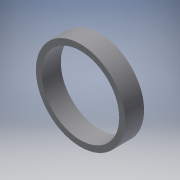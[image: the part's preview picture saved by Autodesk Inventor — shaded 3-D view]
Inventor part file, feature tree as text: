
AUTODESK INVENTOR PART (.ipt)
format: ipt  version: 2017 (Build 210142000, 142)  size: 103,424 bytes
history: native  units: in
note: dims shown in document units (in); Inventor stores cm internally (conversion verified against a paired STEP export)
features: other x3, reference x2, sketch x1, plane x1, extrude x1
ambient origin geometry x8: Origin, YZ Plane, XZ Plane, XY Plane, X Axis, Y Axis, Z Axis, Center Point
bodies: Solid1 (feature_tree)
feature tree (8):
  sketch  "Sketch1"  dims[d0=0.48in d1=1.0in d2=0.0in]
  plane  "Work Plane1"
  extrude  "Extrusion1"  Depth=1.0in TaperAngle=0.0deg
  reference  "Reference1"
  reference  "Reference2"
  other  "<userpath>\Documents\Inventor\PixyCam and Gimbal\PIXYWITHRING.iam"
  other  "PIXYWITHRING.iam"
  other  "PixyCamKinda:1"
